# Revit family: Скамейка стальная «Лесенка 3-х ярусная» Арт 20901
name_source: partatom
category: Антураж
revit_build: Autodesk Revit 2018 (Build: 20180423_1000(x64)
units: mm (PartAtom-declared; Revit-internal decimal feet)

## family parameters
Всегда вертикально = Да
Источник визуального образа = Геометрия семейства
На основе рабочей плоскости = Нет
Общий = Нет
При загрузке вырезать с полостями = Нет
Точка расчета площади = Нет

## types (2) — shared parameters
URL = https://hobbyka.ru
Артикул товара = Арт. 20901
Высота = 1000 мм
Группа модели = Скамейки
Длина = 1800 мм
Изготовитель = ООО «Хоббика»
Изображение типоразмера = Скамейка стальная «Лесенка 3-х ярусная» Арт 20901.jpg
Материал изделия = Сталь, дерево
Цвет опор = Сталь
Ширина = 1860 мм

## per-type parameters (varying)
| type | Версия 1,86 м (лиственница) | Версия 1,86 м (сосна) | Описание | Цвет лавки |
| Версия 1,86 м (сосна) | Нет | Да | Скамейка стальная «Лесенка 3-х ярусная». Версия 1,86 м (сосна) | Сосна |
| Версия 1,86 м (лиственница) | Да | Нет | Скамейка стальная «Лесенка 3-х ярусная». Версия 1,86 м (лиственница) | Лиственница |
